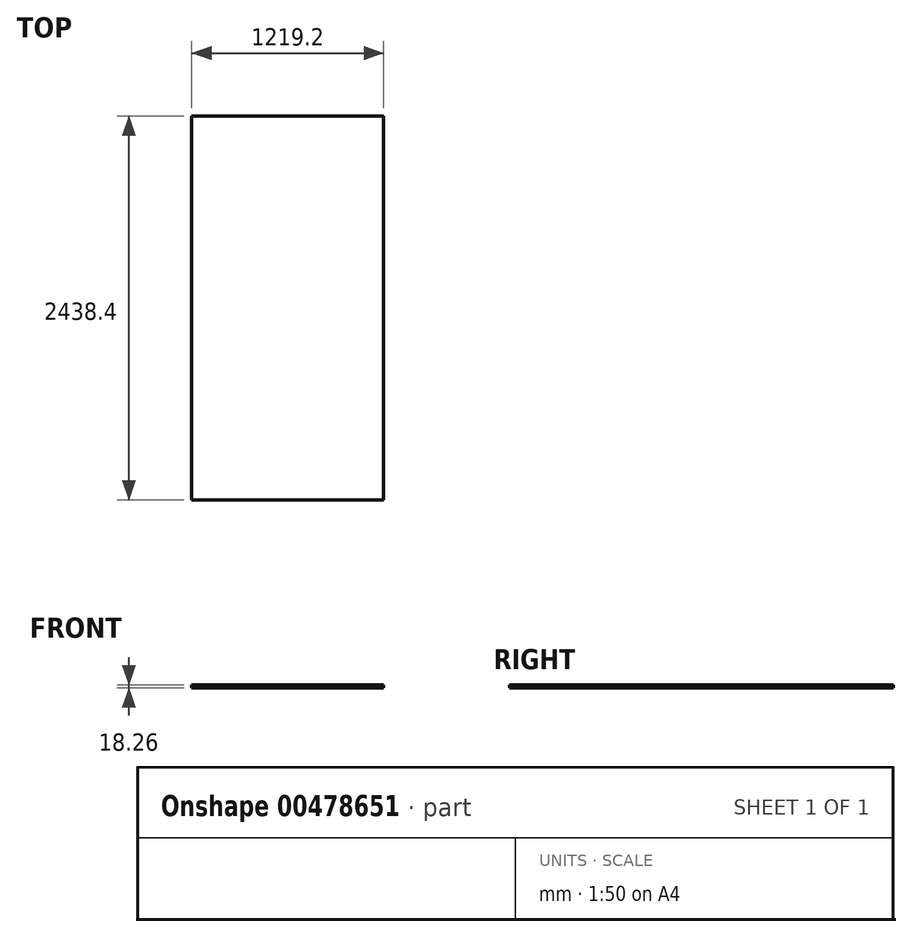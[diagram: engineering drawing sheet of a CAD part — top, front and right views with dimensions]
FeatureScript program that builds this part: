
annotation { "Feature Type Name" : "Feature", "Feature Type Description" : "" }
export const myFeature = defineFeature(function(context is Context, id is Id, definition is map)
    precondition{}
    {
        {
            var Q0;
            Q0=qCreatedBy(makeId("Top.planeOp"),FACE);
            var sketch = newSketch(context, id + "F0", { "sketchPlane" : qUnion([Q0])});
            skLineSegment(sketch, "E0.bottom", {"start": v(0, 0) * mm, "end": v(1219.2, 0) * mm});
            skLineSegment(sketch, "E0.top", {"start": v(0, 2438.4) * mm, "end": v(1219.2, 2438.4) * mm});
            skLineSegment(sketch, "E0.left", {"start": v(0, 0) * mm, "end": v(0, 2438.4) * mm});
            skLineSegment(sketch, "E0.right", {"start": v(1219.2, 0) * mm, "end": v(1219.2, 2438.4) * mm});
            skSolve(sketch);
        }
        {
            var Q0;
            Q0=makeQuery(id+"F0.imprint","IMPRINT",FACE,{"disambiguationData":[TD([[makeQuery(id+"F0.imprint","IMPRINT",EDGE,{"derivedFrom":sQuery(id+"F0.wireOp",EDGE,"E0.bottom")}),1.0]])]});
            extrude(context, id + "F1", {"entities" : qUnion([Q0]), "depth" : 18.26 * mm});
        }
    });
